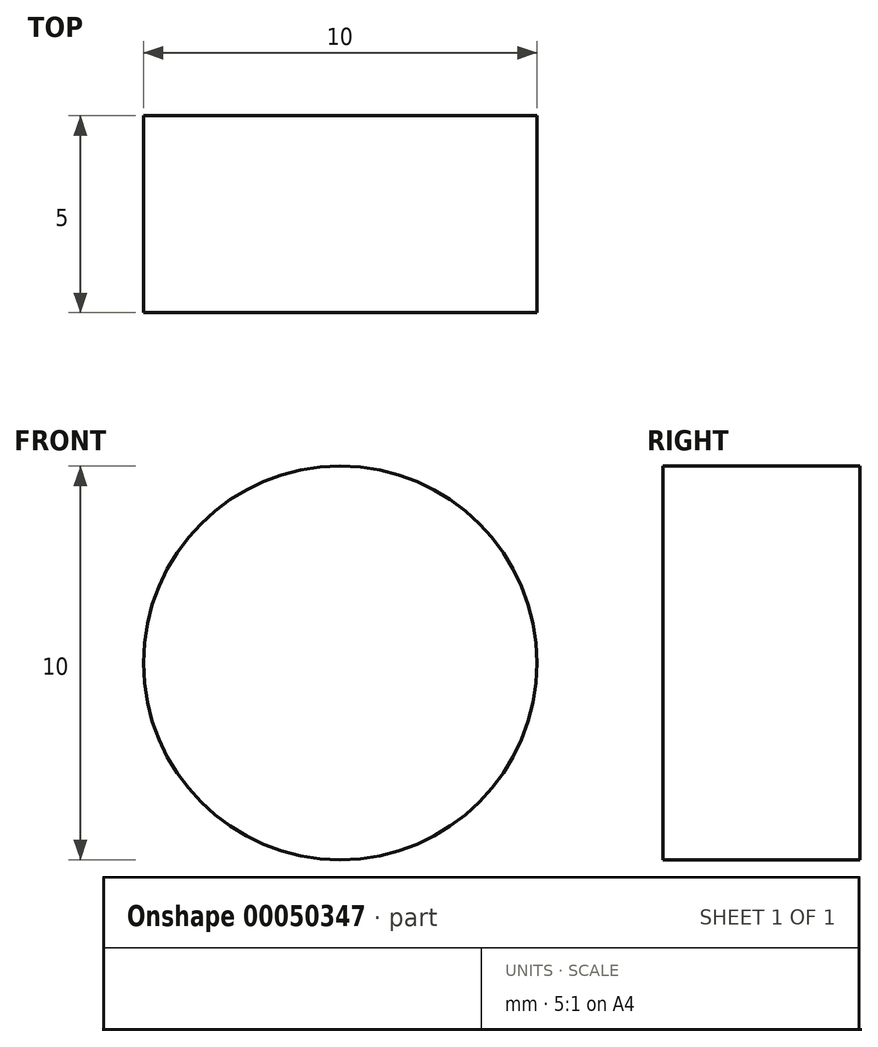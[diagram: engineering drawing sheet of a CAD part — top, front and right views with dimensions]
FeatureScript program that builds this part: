
annotation { "Feature Type Name" : "Feature", "Feature Type Description" : "" }
export const myFeature = defineFeature(function(context is Context, id is Id, definition is map)
    precondition{}
    {
        {
            var Q0;
            Q0=qCreatedBy(makeId("Front.planeOp"),FACE);
            var sketch = newSketch(context, id + "F0", { "sketchPlane" : qUnion([Q0])});
            skCircle(sketch, "E0", {"center": v(0, 0) * mm, "radius": 5 * mm});
            skSolve(sketch);
        }
        {
            var Q0;
            Q0=makeQuery(id+"F0.imprint","IMPRINT",FACE,{"disambiguationData":[TD([[makeQuery(id+"F0.imprint","IMPRINT",EDGE,{"derivedFrom":sQuery(id+"F0.wireOp",EDGE,"E0")}),1.0]])]});
            extrude(context, id + "F1", {"entities" : qUnion([Q0]), "depth" : 5 * mm});
        }
    });
